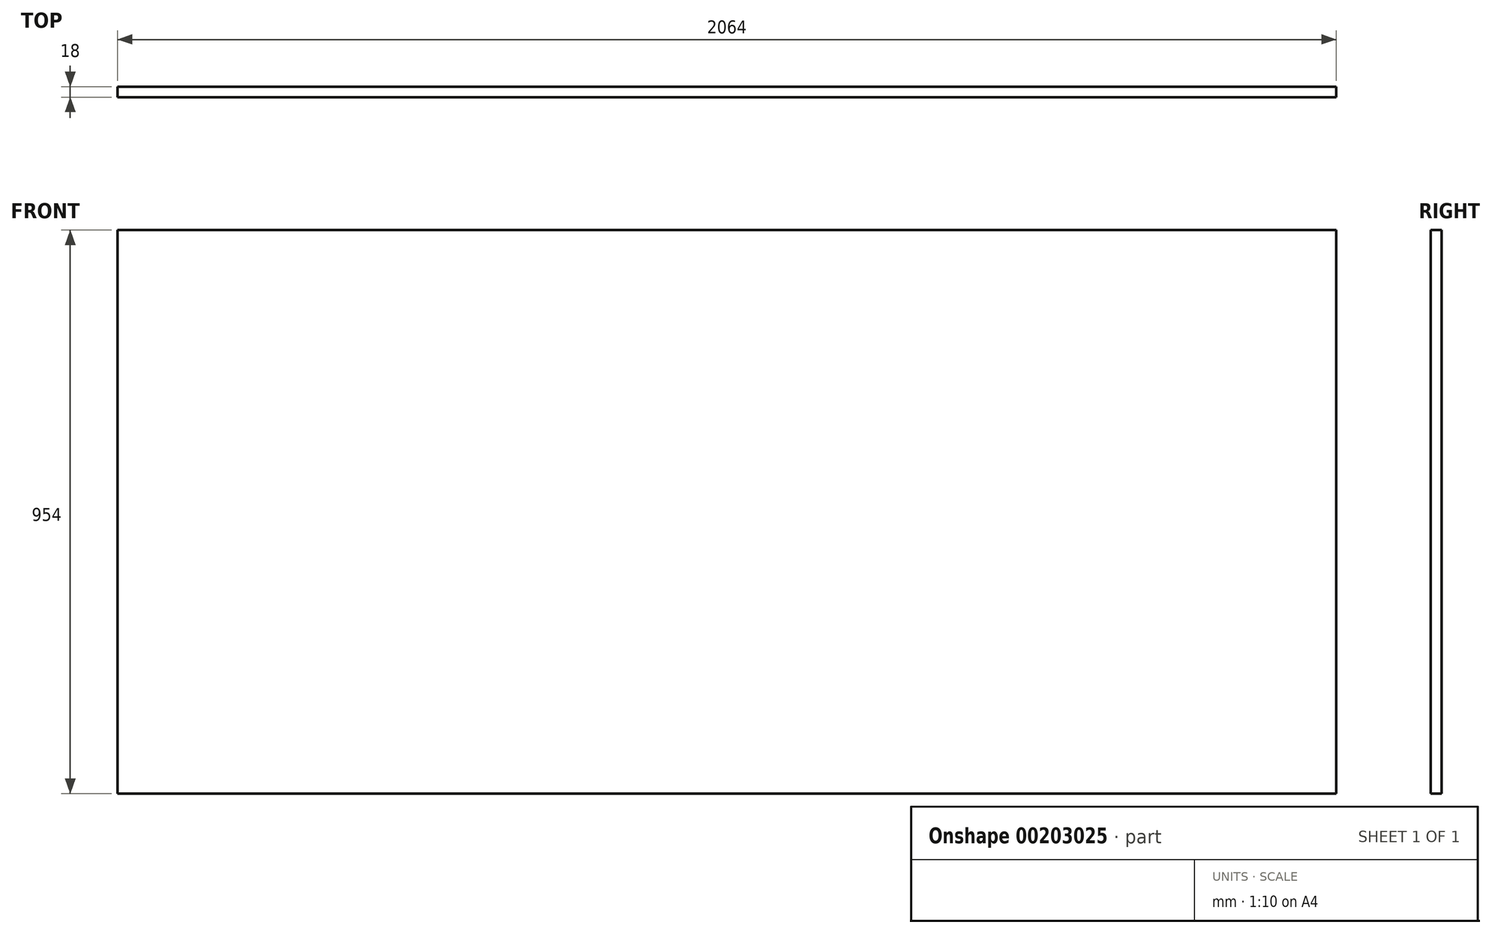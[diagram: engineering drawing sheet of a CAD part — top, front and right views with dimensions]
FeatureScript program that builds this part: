
annotation { "Feature Type Name" : "Feature", "Feature Type Description" : "" }
export const myFeature = defineFeature(function(context is Context, id is Id, definition is map)
    precondition{}
    {
        {
            var Q0;
            Q0=qCreatedBy(makeId("Front.planeOp"),FACE);
            var sketch = newSketch(context, id + "F0", { "sketchPlane" : qUnion([Q0])});
            skLineSegment(sketch, "E0.bottom", {"start": v(-1032, -477) * mm, "end": v(1032, -477) * mm});
            skLineSegment(sketch, "E0.top", {"start": v(-1032, 477) * mm, "end": v(1032, 477) * mm});
            skLineSegment(sketch, "E0.left", {"start": v(-1032, -477) * mm, "end": v(-1032, 477) * mm});
            skLineSegment(sketch, "E0.right", {"start": v(1032, -477) * mm, "end": v(1032, 477) * mm});
            skPoint(sketch, "E0.middle", {"position": v(0, 0) * mm});
            skSolve(sketch);
        }
        {
            var Q0;
            Q0=makeQuery(id+"F0.imprint","IMPRINT",FACE,{"disambiguationData":[TD([[makeQuery(id+"F0.imprint","IMPRINT",EDGE,{"derivedFrom":sQuery(id+"F0.wireOp",EDGE,"E0.bottom")}),1.0]])]});
            extrude(context, id + "F1", {"entities" : qUnion([Q0]), "depth" : 18 * mm});
        }
    });
